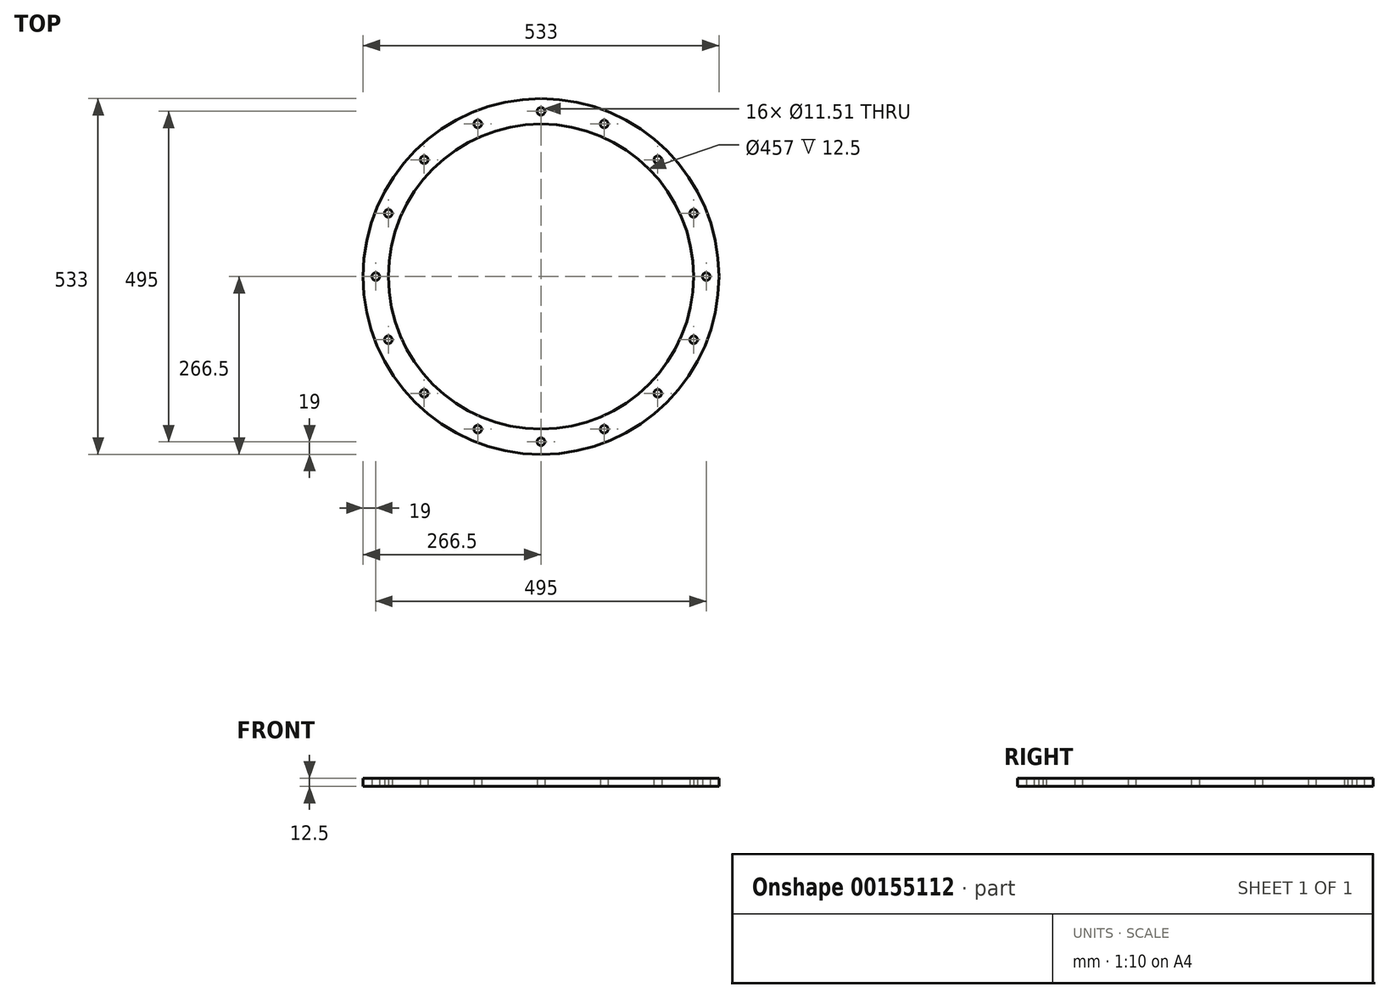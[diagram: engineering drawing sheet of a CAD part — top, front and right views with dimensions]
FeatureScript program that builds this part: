
annotation { "Feature Type Name" : "Feature", "Feature Type Description" : "" }
export const myFeature = defineFeature(function(context is Context, id is Id, definition is map)
    precondition{}
    {
        {
            var Q0;
            Q0=qCreatedBy(makeId("Top.planeOp"),FACE);
            var sketch = newSketch(context, id + "F0", { "sketchPlane" : qUnion([Q0])});
            skCircle(sketch, "E0", {"center": v(0, 0) * mm, "radius": 266.5 * mm});
            skCircle(sketch, "E1", {"center": v(0, 0) * mm, "radius": 228.5 * mm});
            skSolve(sketch);
        }
        {
            var Q0;
            Q0 = qSketchRegion(id + "F0", true);
            extrude(context, id + "F1", {"entities" : qUnion([Q0]), "depth" : 12.5 * mm});
        }
        {
            var Q0;
            Q0=makeQuery(id+"F1.opExtrude","CAP_FACE",FACE,{"disambiguationData":[OSD([sQuery(id+"F0.wireOp",EDGE,"E0"),sQuery(id+"F0.wireOp",EDGE,"E1")])],"isStart":false});
            var sketch = newSketch(context, id + "F2", { "sketchPlane" : qUnion([Q0])});
            skCircle(sketch, "E2", {"center": v(0, 0) * mm, "radius": 247.5 * mm});
            skLineSegment(sketch, "E3", {"start": v(0, 247.5) * mm, "end": v(0, 294.17) * mm});
            skLineSegment(sketch, "E4.1.0", {"start": v(-94.71, 228.66) * mm, "end": v(-112.57, 271.78) * mm});
            skLineSegment(sketch, "E4.2.0", {"start": v(-175, 175) * mm, "end": v(-208, 208) * mm});
            skLineSegment(sketch, "E4.3.0", {"start": v(-228.66, 94.71) * mm, "end": v(-271.78, 112.57) * mm});
            skLineSegment(sketch, "E4.4.0", {"start": v(-247.5, 0) * mm, "end": v(-294.17, 0) * mm});
            skLineSegment(sketch, "E4.5.0", {"start": v(-228.66, -94.71) * mm, "end": v(-271.78, -112.57) * mm});
            skLineSegment(sketch, "E4.6.0", {"start": v(-175, -175) * mm, "end": v(-208, -208) * mm});
            skLineSegment(sketch, "E4.7.0", {"start": v(-94.71, -228.66) * mm, "end": v(-112.57, -271.78) * mm});
            skLineSegment(sketch, "E4.8.0", {"start": v(0, -247.5) * mm, "end": v(0, -294.17) * mm});
            skLineSegment(sketch, "E4.9.0", {"start": v(94.71, -228.66) * mm, "end": v(112.57, -271.78) * mm});
            skLineSegment(sketch, "E4.10.0", {"start": v(175, -175) * mm, "end": v(208, -208) * mm});
            skLineSegment(sketch, "E4.11.0", {"start": v(228.66, -94.71) * mm, "end": v(271.78, -112.57) * mm});
            skLineSegment(sketch, "E4.12.0", {"start": v(247.5, 0) * mm, "end": v(294.17, 0) * mm});
            skLineSegment(sketch, "E4.13.0", {"start": v(228.66, 94.71) * mm, "end": v(271.78, 112.57) * mm});
            skLineSegment(sketch, "E4.14.0", {"start": v(175, 175) * mm, "end": v(208, 208) * mm});
            skLineSegment(sketch, "E4.15.0", {"start": v(94.71, 228.66) * mm, "end": v(112.57, 271.78) * mm});
            skSolve(sketch);
        }
        {
            var Q0;
            Q0=sQuery(id+"F2.wireOp",VERTEX,"E4.1.0.start");
            var Q1;
            Q1=sQuery(id+"F2.wireOp",VERTEX,"E3.start");
            var Q2;
            Q2=sQuery(id+"F2.wireOp",VERTEX,"E4.15.0.start");
            var Q3;
            Q3=sQuery(id+"F2.wireOp",VERTEX,"E4.14.0.start");
            var Q4;
            Q4=sQuery(id+"F2.wireOp",VERTEX,"E4.13.0.start");
            var Q5;
            Q5=sQuery(id+"F2.wireOp",VERTEX,"E4.12.0.start");
            var Q6;
            Q6=sQuery(id+"F2.wireOp",VERTEX,"E4.11.0.start");
            var Q7;
            Q7=sQuery(id+"F2.wireOp",VERTEX,"E4.10.0.start");
            var Q8;
            Q8=sQuery(id+"F2.wireOp",VERTEX,"E4.9.0.start");
            var Q9;
            Q9=sQuery(id+"F2.wireOp",VERTEX,"E4.8.0.start");
            var Q10;
            Q10=sQuery(id+"F2.wireOp",VERTEX,"E4.7.0.start");
            var Q11;
            Q11=sQuery(id+"F2.wireOp",VERTEX,"E4.6.0.start");
            var Q12;
            Q12=sQuery(id+"F2.wireOp",VERTEX,"E4.5.0.start");
            var Q13;
            Q13=sQuery(id+"F2.wireOp",VERTEX,"E4.4.0.start");
            var Q14;
            Q14=sQuery(id+"F2.wireOp",VERTEX,"E4.3.0.start");
            var Q15;
            Q15=sQuery(id+"F2.wireOp",VERTEX,"E4.2.0.start");
            var Q16;
            Q16=makeQuery(id+"F1.opExtrude","SWEPT_BODY",BODY,{"disambiguationData":[OSD([sQuery(id+"F0.wireOp",EDGE,"E0"),sQuery(id+"F0.wireOp",EDGE,"E1")])]});
            hole(context, id + "F3", {"style" : HoleStyle.SIMPLE, "endStyle" : HoleEndStyle.THROUGH, "standardTappedOrClearance" : lookupTablePath({ "standard" : "ANSI", "engagement" : "75%", "pitch" : "20 tpi", "size" : "1/2", "type" : "Tapped" }), "standardBlindInLast" : lookupTablePath({ "standard" : "ANSI", "engagement" : "75%", "pitch" : "20 tpi", "size" : "1/2", "type" : "Tapped" }), "holeDiameter" : 11.5 * mm, "locations" : qUnion([Q0, Q1, Q2, Q3, Q4, Q5, Q6, Q7, Q8, Q9, Q10, Q11, Q12, Q13, Q14, Q15]), "scope" : qUnion([Q16]), "isTappedThrough" : true, "majorDiameter" : 12.7 * mm, "showTappedDepth" : true, "startStyle" : HoleStartStyle.PART});
        }
    });
